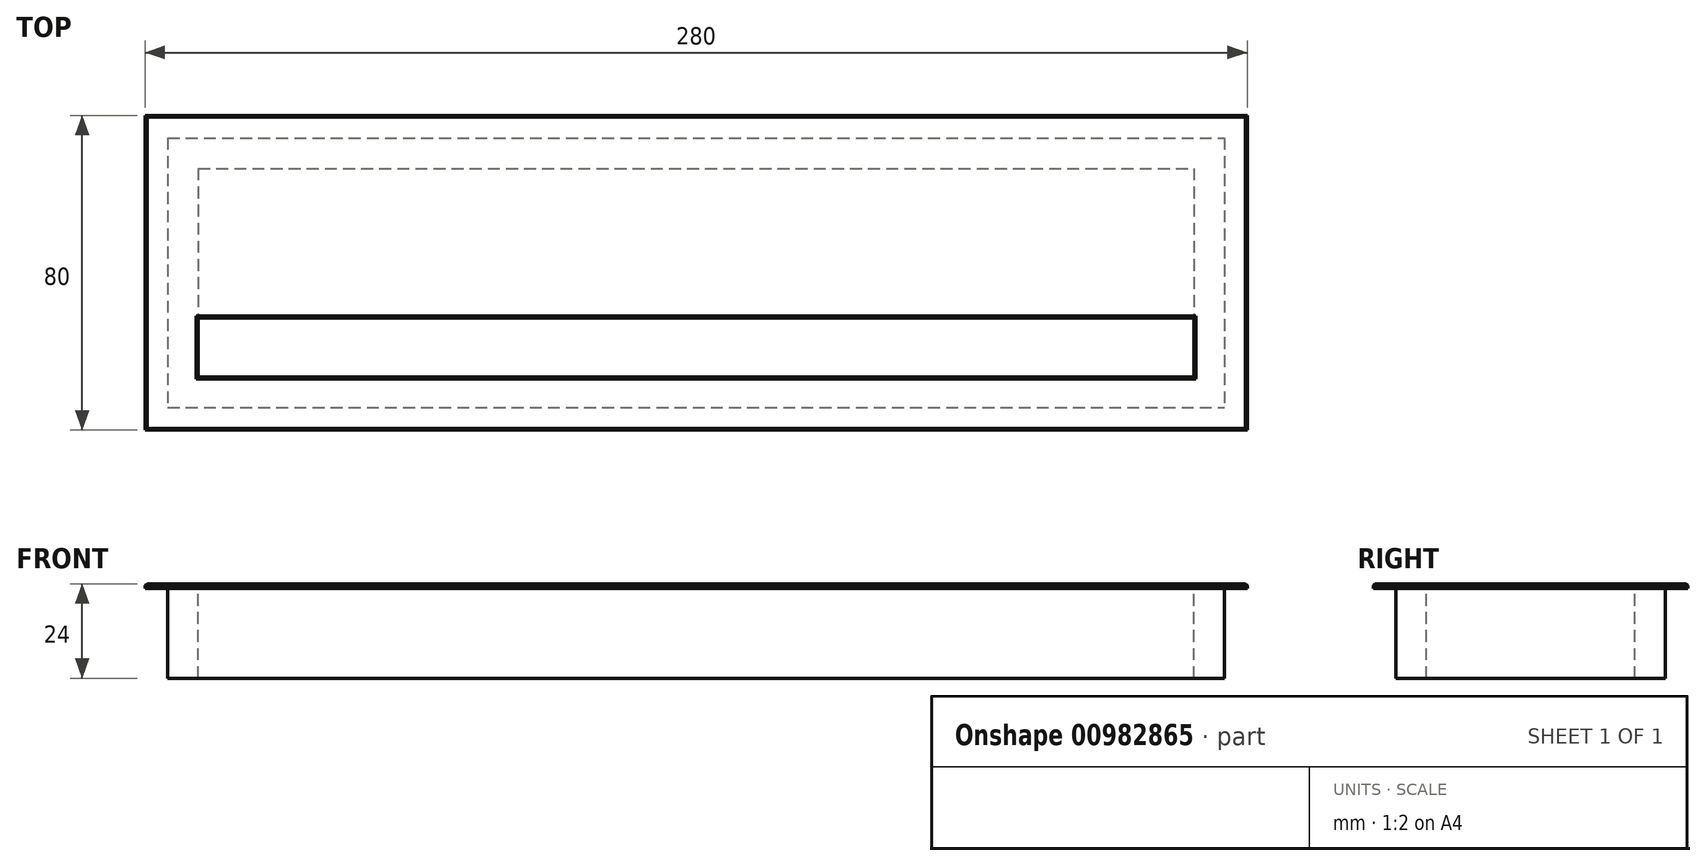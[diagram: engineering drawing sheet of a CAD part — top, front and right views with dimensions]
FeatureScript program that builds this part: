
annotation { "Feature Type Name" : "Feature", "Feature Type Description" : "" }
export const myFeature = defineFeature(function(context is Context, id is Id, definition is map)
    precondition{}
    {
        {
            var Q0;
            Q0=qCreatedBy(makeId("Top.planeOp"),FACE);
            var sketch = newSketch(context, id + "F0", { "sketchPlane" : qUnion([Q0])});
            skLineSegment(sketch, "E0.bottom", {"start": v(-179.45, 41.33) * mm, "end": v(100.55, 41.33) * mm});
            skLineSegment(sketch, "E0.top", {"start": v(-179.45, -38.67) * mm, "end": v(100.55, -38.67) * mm});
            skLineSegment(sketch, "E0.left", {"start": v(-179.45, 41.33) * mm, "end": v(-179.45, -38.67) * mm});
            skLineSegment(sketch, "E0.right", {"start": v(100.55, 41.33) * mm, "end": v(100.55, -38.67) * mm});
            skLineSegment(sketch, "E1.bottom", {"start": v(-165.95, 27.83) * mm, "end": v(87.05, 27.83) * mm});
            skLineSegment(sketch, "E1.top", {"start": v(-165.95, -25.17) * mm, "end": v(87.05, -25.17) * mm});
            skLineSegment(sketch, "E1.left", {"start": v(-165.95, 27.83) * mm, "end": v(-165.95, -25.17) * mm});
            skLineSegment(sketch, "E1.right", {"start": v(87.05, 27.83) * mm, "end": v(87.05, -25.17) * mm});
            skLineSegment(sketch, "E2.bottom", {"start": v(-173.7, 35.58) * mm, "end": v(94.8, 35.58) * mm});
            skLineSegment(sketch, "E2.top", {"start": v(-173.7, -32.92) * mm, "end": v(94.8, -32.92) * mm});
            skLineSegment(sketch, "E2.left", {"start": v(-173.7, 35.58) * mm, "end": v(-173.7, -32.92) * mm});
            skLineSegment(sketch, "E2.right", {"start": v(94.8, 35.58) * mm, "end": v(94.8, -32.92) * mm});
            skLineSegment(sketch, "E3", {"start": v(-165.95, -10.17) * mm, "end": v(87.05, -10.17) * mm});
            skSolve(sketch);
        }
        {
            var Q0;
            {var subQ0=sQuery(id+"F0.wireOp",EDGE,"E1.bottom");Q0=makeQuery(id+"F0.imprint","IMPRINT",FACE,{"disambiguationData":[TD([[makeQuery(id+"F0.imprint","IMPRINT",EDGE,{"derivedFrom":subQ0}),-1.0]])]});}
            var Q1;
            Q1=makeQuery(id+"F0.imprint","IMPRINT",FACE,{"disambiguationData":[TD([[makeQuery(id+"F0.imprint","IMPRINT",EDGE,{"derivedFrom":sQuery(id+"F0.wireOp",EDGE,"E0.bottom")}),-1.0]])]});
            extrude(context, id + "F1", {"entities" : qUnion([Q0, Q1]), "oppositeDirection" : true, "depth" : 1.2 * mm, "offsetDistance" : 25 * mm});
        }
        {
            var Q0;
            {var subQ4=sQuery(id+"F0.wireOp",EDGE,"E1.bottom");Q0=makeQuery(id+"F0.imprint","IMPRINT",FACE,{"disambiguationData":[TD([[makeQuery(id+"F0.imprint","IMPRINT",EDGE,{"derivedFrom":subQ4}),1.0]])]});}
            extrude(context, id + "F2", {"entities" : qUnion([Q0]), "oppositeDirection" : true, "depth" : 24 * mm, "offsetDistance" : 25 * mm});
        }
        {
            var Q0;
            Q0=makeQuery(id+"F2.opExtrude","SWEPT_BODY",BODY,{"disambiguationData":[OSD([sQuery(id+"F0.wireOp",EDGE,"E1.bottom"),sQuery(id+"F0.wireOp",EDGE,"E1.top"),sQuery(id+"F0.wireOp",EDGE,"E1.left"),sQuery(id+"F0.wireOp",EDGE,"E1.right"),sQuery(id+"F0.wireOp",EDGE,"E2.bottom"),sQuery(id+"F0.wireOp",EDGE,"E2.top"),sQuery(id+"F0.wireOp",EDGE,"E2.left"),sQuery(id+"F0.wireOp",EDGE,"E2.right")])]});
            var Q1;
            Q1=makeQuery(id+"F1.opExtrude","SWEPT_BODY",BODY,{"disambiguationData":[OSD([sQuery(id+"F0.wireOp",EDGE,"E1.bottom"),sQuery(id+"F0.wireOp",EDGE,"E1.left"),sQuery(id+"F0.wireOp",EDGE,"E1.right"),sQuery(id+"F0.wireOp",EDGE,"E3")])]});
            var Q2;
            Q2=makeQuery(id+"F1.opExtrude","SWEPT_BODY",BODY,{"disambiguationData":[OSD([sQuery(id+"F0.wireOp",EDGE,"E0.bottom"),sQuery(id+"F0.wireOp",EDGE,"E0.top"),sQuery(id+"F0.wireOp",EDGE,"E0.left"),sQuery(id+"F0.wireOp",EDGE,"E0.right"),sQuery(id+"F0.wireOp",EDGE,"E2.bottom"),sQuery(id+"F0.wireOp",EDGE,"E2.top"),sQuery(id+"F0.wireOp",EDGE,"E2.left"),sQuery(id+"F0.wireOp",EDGE,"E2.right")])]});
            booleanBodies(context, id + "F3", {"operationType" : BooleanOperationType.UNION, "tools" : qUnion([Q0, Q1, Q2])});
        }
        {
            var Q0;
            Q0=makeQuery(id+"F1.opExtrude","CAP_EDGE",EDGE,{"disambiguationData":[OSD([sQuery(id+"F0.wireOp",EDGE,"E0.top")])],"isStart":true});
            var Q1;
            Q1=makeQuery(id+"F1.opExtrude","CAP_EDGE",EDGE,{"disambiguationData":[OSD([sQuery(id+"F0.wireOp",EDGE,"E0.left")])],"isStart":true});
            var Q2;
            Q2=makeQuery(id+"F1.opExtrude","CAP_EDGE",EDGE,{"disambiguationData":[OSD([sQuery(id+"F0.wireOp",EDGE,"E0.bottom")])],"isStart":true});
            var Q3;
            Q3=makeQuery(id+"F1.opExtrude","CAP_EDGE",EDGE,{"disambiguationData":[OSD([sQuery(id+"F0.wireOp",EDGE,"E0.right")])],"isStart":true});
            var Q4;
            Q4=makeQuery(id+"F1.opExtrude","CAP_EDGE",EDGE,{"disambiguationData":[OSD([sQuery(id+"F0.wireOp",EDGE,"E3")])],"isStart":true});
            var Q5;
            Q5=makeQuery(id+"F2.opExtrude","CAP_EDGE",EDGE,{"disambiguationData":[OSD([sQuery(id+"F0.wireOp",EDGE,"E1.right")])],"isStart":true});
            var Q6;
            Q6=makeQuery(id+"F2.opExtrude","CAP_EDGE",EDGE,{"disambiguationData":[OSD([sQuery(id+"F0.wireOp",EDGE,"E1.top")])],"isStart":true});
            var Q7;
            {var subQ0=sQuery(id+"F0.wireOp",EDGE,"E2.right");var subQ1=sQuery(id+"F0.wireOp",EDGE,"E2.left");var subQ2=sQuery(id+"F0.wireOp",EDGE,"E2.top");var subQ3=sQuery(id+"F0.wireOp",EDGE,"E2.bottom");var subQ4=sQuery(id+"F0.wireOp",EDGE,"E1.right");var subQ5=sQuery(id+"F0.wireOp",EDGE,"E1.left");var subQ6=sQuery(id+"F0.wireOp",EDGE,"E1.bottom");Q7=makeQuery(id+"F3.opBoolean","MERGE",FACE,{"derivedFrom":[makeQuery(id+"F1.opExtrude","CAP_FACE",FACE,{"disambiguationData":[OSD([sQuery(id+"F0.wireOp",EDGE,"E0.bottom"),sQuery(id+"F0.wireOp",EDGE,"E0.top"),sQuery(id+"F0.wireOp",EDGE,"E0.left"),sQuery(id+"F0.wireOp",EDGE,"E0.right"),subQ3,subQ2,subQ1,subQ0])],"isStart":true}),makeQuery(id+"F1.opExtrude","CAP_FACE",FACE,{"disambiguationData":[OSD([subQ6,subQ5,subQ4,sQuery(id+"F0.wireOp",EDGE,"E3")])],"isStart":true}),makeQuery(id+"F2.opExtrude","CAP_FACE",FACE,{"disambiguationData":[OSD([subQ6,sQuery(id+"F0.wireOp",EDGE,"E1.top"),subQ5,subQ4,subQ3,subQ2,subQ1,subQ0])],"isStart":true})]});}
            chamfer(context, id + "F4", {"entities" : qUnion([Q0, Q1, Q2, Q3, Q4, Q5, Q6, Q7]), "width" : 0.5 * mm, "tangentPropagation" : true});
        }
    });
